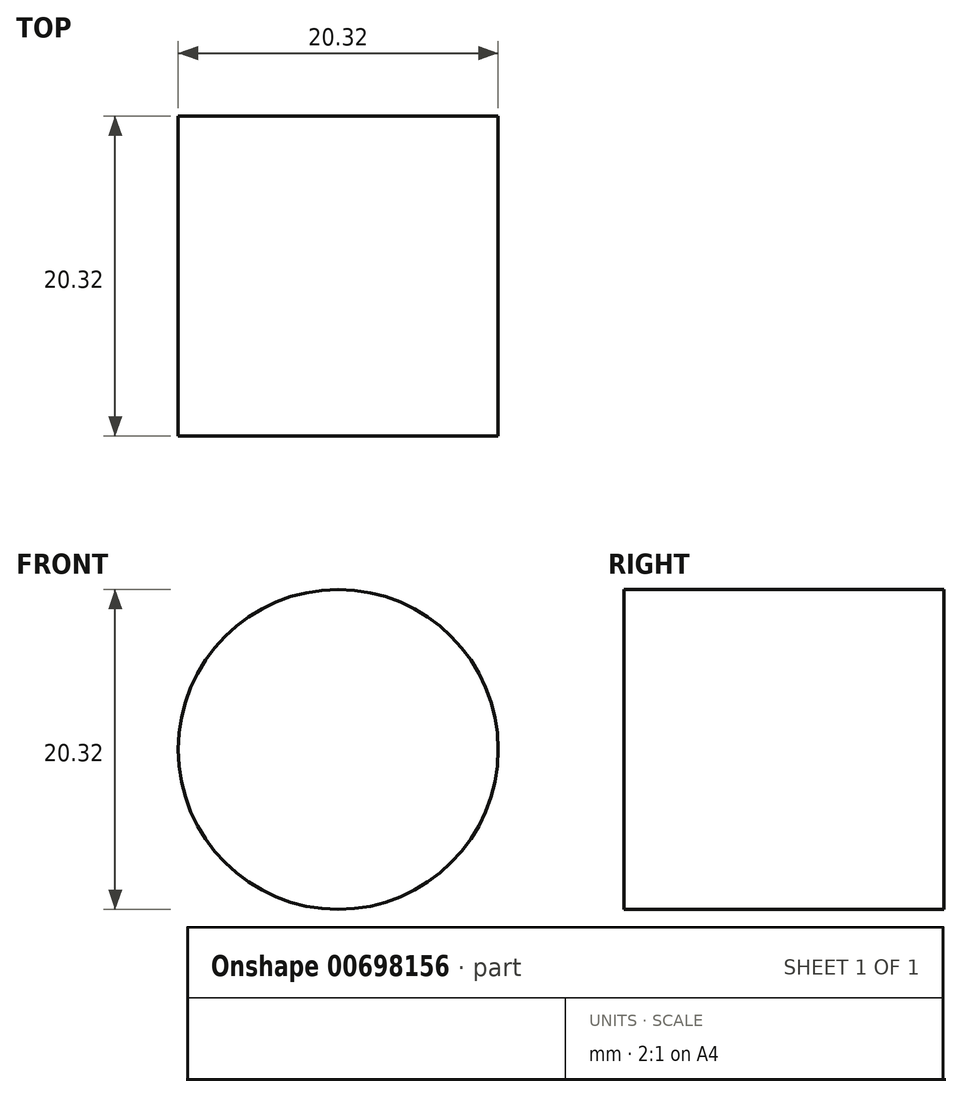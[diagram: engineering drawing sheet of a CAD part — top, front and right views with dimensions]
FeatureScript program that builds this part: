
annotation { "Feature Type Name" : "Feature", "Feature Type Description" : "" }
export const myFeature = defineFeature(function(context is Context, id is Id, definition is map)
    precondition{}
    {
        {
            var Q0;
            Q0=qCreatedBy(makeId("Front.planeOp"),FACE);
            var sketch = newSketch(context, id + "F0", { "sketchPlane" : qUnion([Q0])});
            skCircle(sketch, "E0", {"center": v(0, 0) * mm, "radius": 10.16 * mm});
            skSolve(sketch);
        }
        {
            var Q0;
            Q0=qSketchRegion(id+"F0",true);
            extrude(context, id + "F1", {"entities" : qUnion([Q0]), "depth" : 20.32 * mm, "offsetDistance" : 25.4 * mm});
        }
    });
